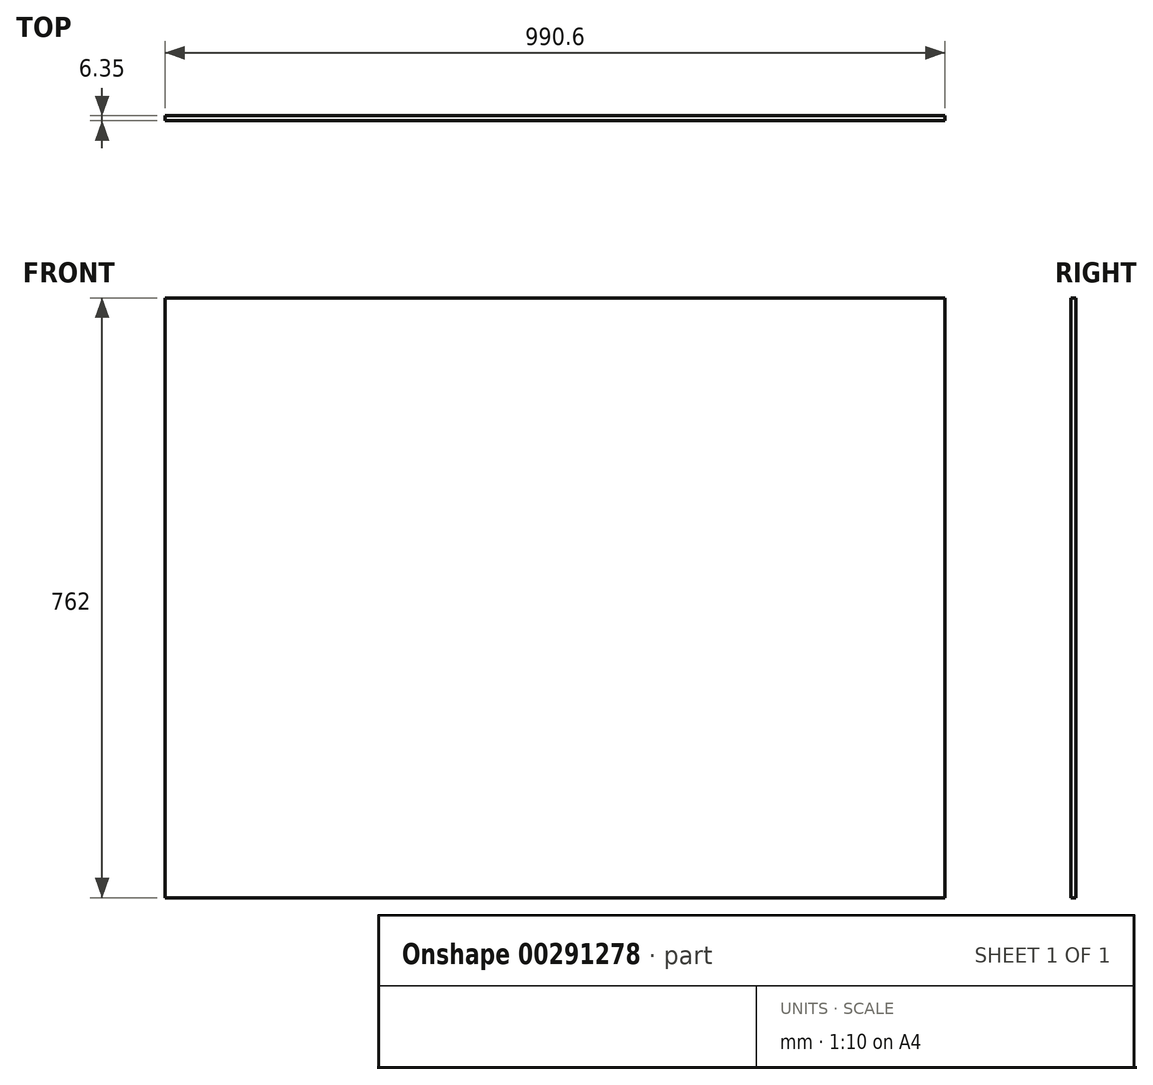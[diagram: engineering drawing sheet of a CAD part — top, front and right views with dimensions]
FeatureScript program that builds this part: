
annotation { "Feature Type Name" : "Feature", "Feature Type Description" : "" }
export const myFeature = defineFeature(function(context is Context, id is Id, definition is map)
    precondition{}
    {
        {
            var Q0;
            Q0=qCreatedBy(makeId("Front.planeOp"),FACE);
            var sketch = newSketch(context, id + "F0", { "sketchPlane" : qUnion([Q0])});
            skLineSegment(sketch, "E0", {"start": v(-495.3, 381) * mm, "end": v(-495.3, -381) * mm});
            skLineSegment(sketch, "E1", {"start": v(-495.3, -381) * mm, "end": v(495.3, -381) * mm});
            skLineSegment(sketch, "E2", {"start": v(495.3, -381) * mm, "end": v(495.3, 381) * mm});
            skLineSegment(sketch, "E3", {"start": v(-495.3, 381) * mm, "end": v(495.3, 381) * mm});
            skSolve(sketch);
        }
        {
            var Q0;
            Q0 = qSketchRegion(id + "F0", true);
            extrude(context, id + "F1", {"entities" : qUnion([Q0]), "depth" : 6.35 * mm});
        }
    });
